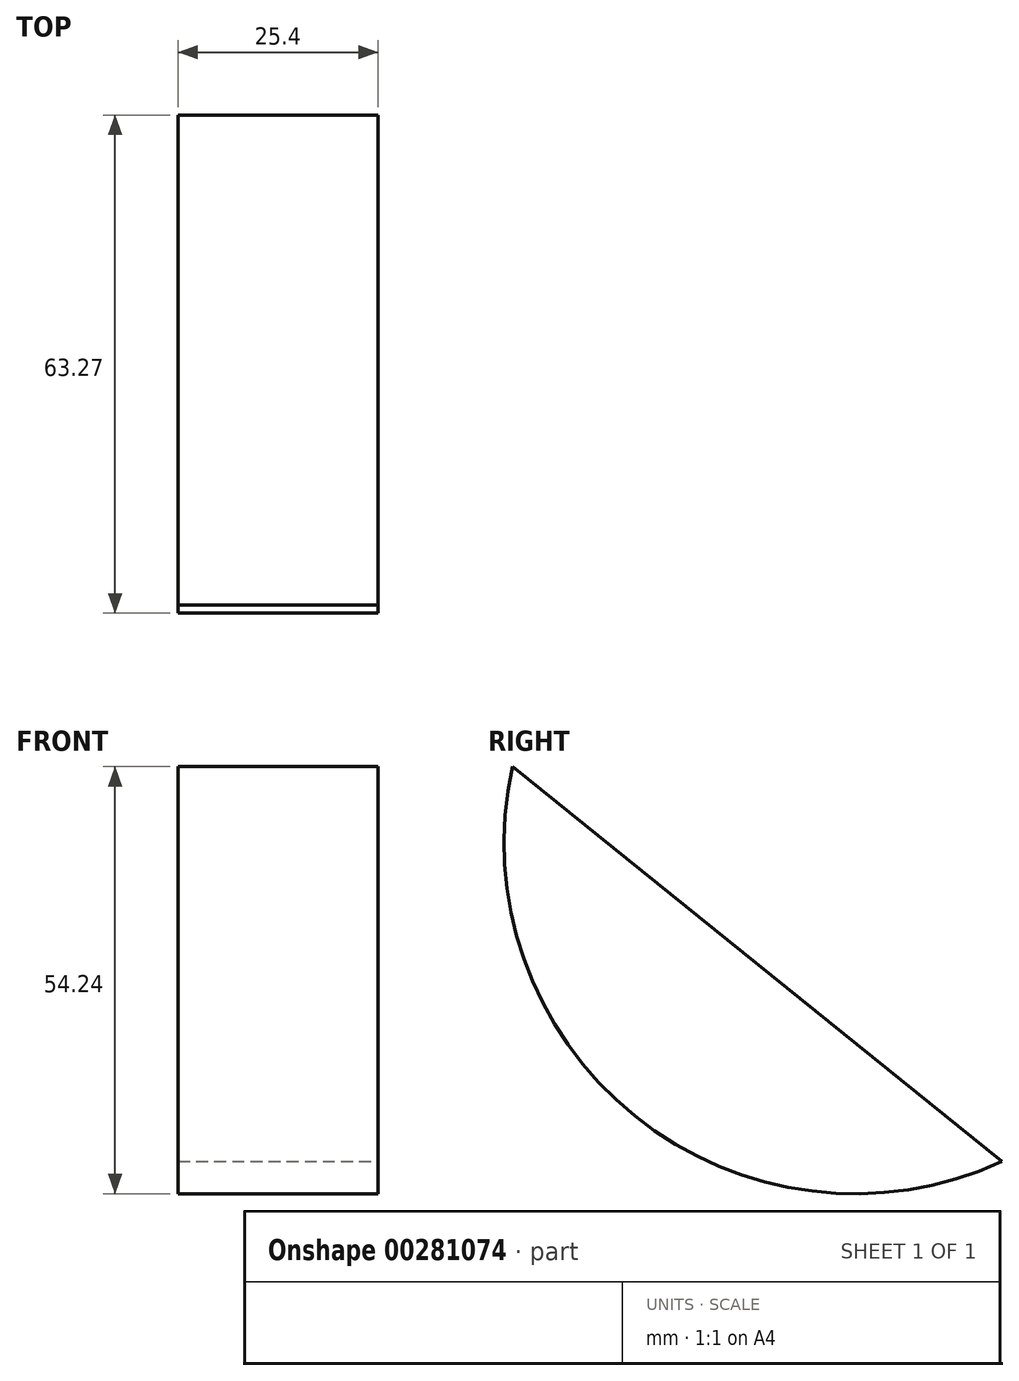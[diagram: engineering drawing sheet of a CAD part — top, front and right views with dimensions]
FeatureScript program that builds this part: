
annotation { "Feature Type Name" : "Feature", "Feature Type Description" : "" }
export const myFeature = defineFeature(function(context is Context, id is Id, definition is map)
    precondition{}
    {
        {
            var Q0;
            Q0=qCreatedBy(makeId("Front.planeOp"),FACE);
            var sketch = newSketch(context, id + "F0", { "sketchPlane" : qUnion([Q0])});
            skLineSegment(sketch, "E0.bottom", {"start": v(-63.5, 63.5) * mm, "end": v(63.5, 63.5) * mm});
            skLineSegment(sketch, "E0.top", {"start": v(-63.5, -63.5) * mm, "end": v(63.5, -63.5) * mm});
            skLineSegment(sketch, "E0.left", {"start": v(-63.5, 63.5) * mm, "end": v(-63.5, -63.5) * mm});
            skLineSegment(sketch, "E0.right", {"start": v(63.5, 63.5) * mm, "end": v(63.5, -63.5) * mm});
            skPoint(sketch, "E0.middle", {"position": v(0, 0) * mm});
            skSolve(sketch);
        }
        {
            var Q0;
            Q0 = qSketchRegion(id + "F0", true);
            extrude(context, id + "F1", {"entities" : qUnion([Q0]), "depth" : 115.57 * mm});
        }
        {
            var Q0;
            Q0=makeQuery(id+"F1.opExtrude","SWEPT_FACE",FACE,{"disambiguationData":[OSD([sQuery(id+"F0.wireOp",EDGE,"E0.right")])]});
            var sketch = newSketch(context, id + "F2", { "sketchPlane" : qUnion([Q0])});
            skArc(sketch, "E1", {"start": v(-106, 50.16) * mm, "mid": v(-90.45, 5.8) * mm, "end": v(-43.8, 0) * mm});
            skLineSegment(sketch, "E2", {"start": v(-106, 50.16) * mm, "end": v(-43.8, 0) * mm});
            skSolve(sketch);
        }
        {
            var Q0;
            Q0=makeQuery(id+"F2.imprint","IMPRINT",FACE,{"disambiguationData":[TD([[makeQuery(id+"F2.imprint","IMPRINT",EDGE,{"derivedFrom":sQuery(id+"F2.wireOp",EDGE,"E1")}),1.0]])]});
            extrude(context, id + "F3", {"entities" : qUnion([Q0]), "operationType" : NewBodyOperationType.INTERSECT, "oppositeDirection" : true, "depth" : 25.4 * mm});
        }
    });
